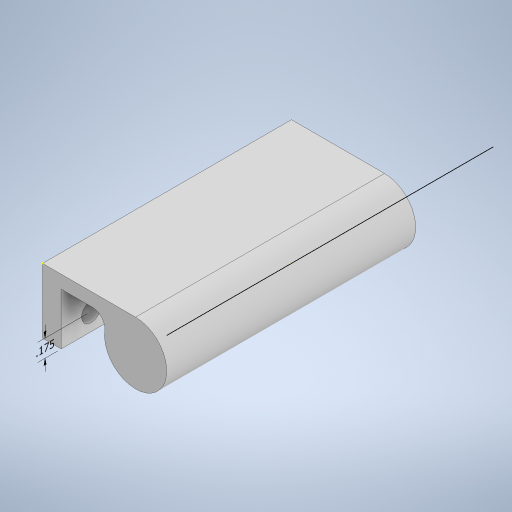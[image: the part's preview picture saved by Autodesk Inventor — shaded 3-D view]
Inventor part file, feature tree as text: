
AUTODESK INVENTOR PART (.ipt)
format: ipt  version: 2024.2 (Build 282272000, 272)  size: 275,456 bytes
history: native  units: in
note: dims shown in document units (in); Inventor stores cm internally (conversion verified against a paired STEP export)
features: sketch x4, extrude x3, other x2
ambient origin geometry x8: Origin, YZ Plane, XZ Plane, XY Plane, X Axis, Y Axis, Z Axis, Center Point
bodies: Solid1 (feature_tree)
feature tree (9):
  other  "Annotations"
  extrude  "Extrusion1"  Depth=0.65in
  extrude  "Extrusion2"  Depth=0.3937in
  extrude  "Extrusion3"  Depth=0.13in
  sketch  "Sketch4"  dims[d15=0.04in d16=0.0in d17=0.935in d18=0.625in d19=0.125in d20=2.5in d21=0.0in d23=0.0278in d24=0.175in]
  sketch  "Sketch1"  dims[d0=2.5in d1=0.65in]
  sketch  "Sketch2"  dims[d4=2.7559in d6=0.3149in d7=0.3937in d9=1.0in d11=0.3in]
  sketch  "Sketch3"  dims[d12=0.1875in d13=0.0in d14=0.13in]
  other  "Linear Dimension 1"
